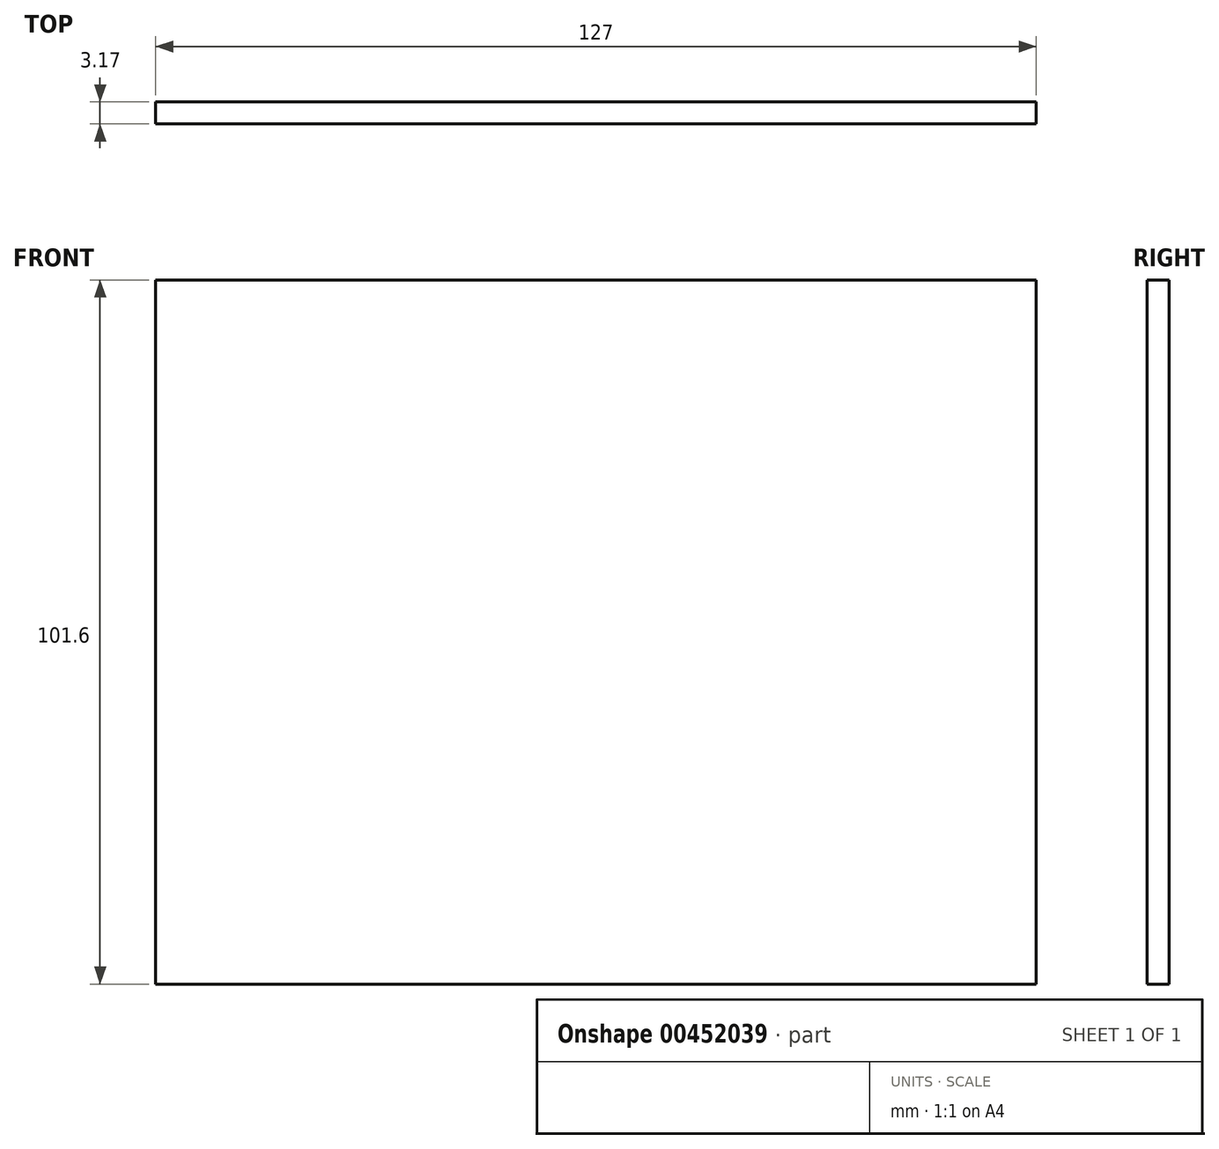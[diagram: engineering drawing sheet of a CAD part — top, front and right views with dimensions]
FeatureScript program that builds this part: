
annotation { "Feature Type Name" : "Feature", "Feature Type Description" : "" }
export const myFeature = defineFeature(function(context is Context, id is Id, definition is map)
    precondition{}
    {
        {
            var Q0;
            Q0=qCreatedBy(makeId("Front.planeOp"),FACE);
            var sketch = newSketch(context, id + "F0", { "sketchPlane" : qUnion([Q0])});
            skLineSegment(sketch, "E0.bottom", {"start": v(-54.72, -41.9) * mm, "end": v(72.28, -41.9) * mm});
            skLineSegment(sketch, "E0.top", {"start": v(-54.72, 59.7) * mm, "end": v(72.28, 59.7) * mm});
            skLineSegment(sketch, "E0.left", {"start": v(-54.72, -41.9) * mm, "end": v(-54.72, 59.7) * mm});
            skLineSegment(sketch, "E0.right", {"start": v(72.28, -41.9) * mm, "end": v(72.28, 59.7) * mm});
            skSolve(sketch);
        }
        {
            var Q0;
            Q0=makeQuery(id+"F0.imprint","IMPRINT",FACE,{"disambiguationData":[TD([[makeQuery(id+"F0.imprint","IMPRINT",EDGE,{"derivedFrom":sQuery(id+"F0.wireOp",EDGE,"E0.bottom")}),1.0]])]});
            extrude(context, id + "F1", {"entities" : qUnion([Q0]), "depth" : 3.17 * mm});
        }
    });
